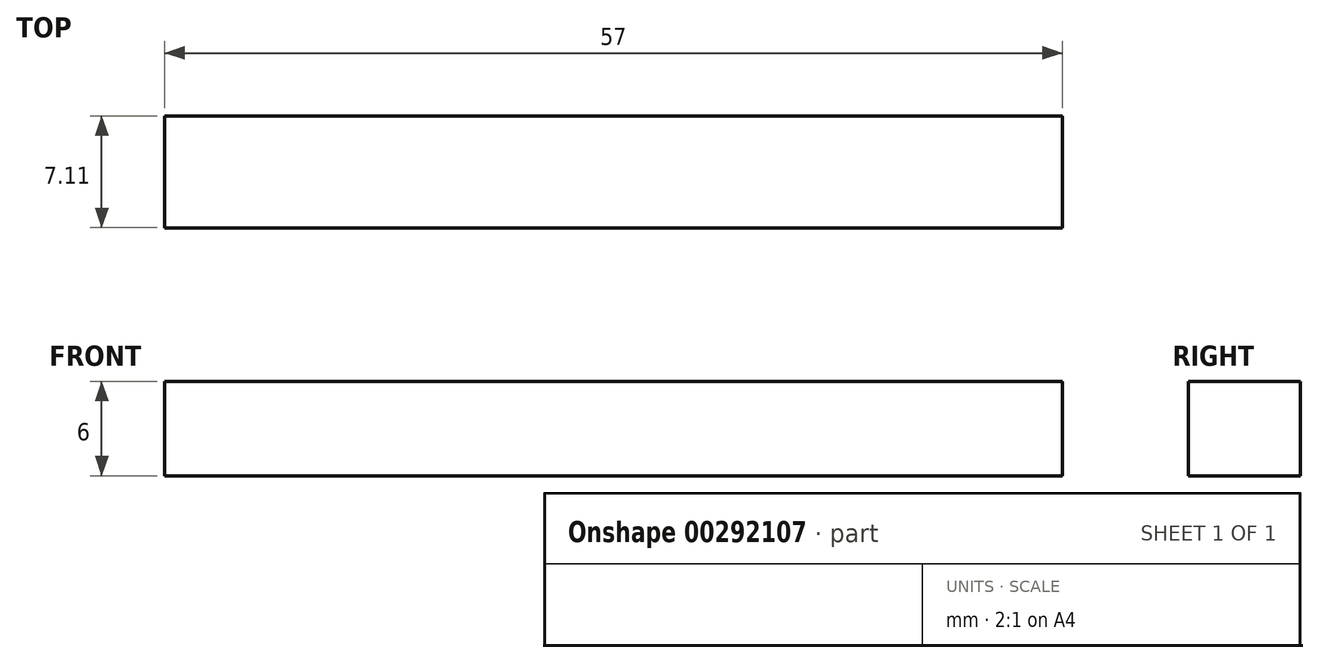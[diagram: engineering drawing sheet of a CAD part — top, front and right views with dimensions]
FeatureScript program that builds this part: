
annotation { "Feature Type Name" : "Feature", "Feature Type Description" : "" }
export const myFeature = defineFeature(function(context is Context, id is Id, definition is map)
    precondition{}
    {
        {
            var Q0;
            Q0=qCreatedBy(makeId("Front.planeOp"),FACE);
            var sketch = newSketch(context, id + "F0", { "sketchPlane" : qUnion([Q0])});
            skLineSegment(sketch, "E0.bottom", {"start": v(0, 0) * mm, "end": v(57, 0) * mm});
            skLineSegment(sketch, "E0.top", {"start": v(0, 6) * mm, "end": v(57, 6) * mm});
            skLineSegment(sketch, "E0.left", {"start": v(0, 0) * mm, "end": v(0, 6) * mm});
            skLineSegment(sketch, "E0.right", {"start": v(57, 0) * mm, "end": v(57, 6) * mm});
            skSolve(sketch);
        }
        {
            var Q0;
            Q0=makeQuery(id+"F0.imprint","IMPRINT",FACE,{"disambiguationData":[TD([[makeQuery(id+"F0.imprint","IMPRINT",EDGE,{"derivedFrom":sQuery(id+"F0.wireOp",EDGE,"E0.bottom")}),1.0]])]});
            extrude(context, id + "F1", {"entities" : qUnion([Q0]), "depth" : 7.11 * mm});
        }
    });
